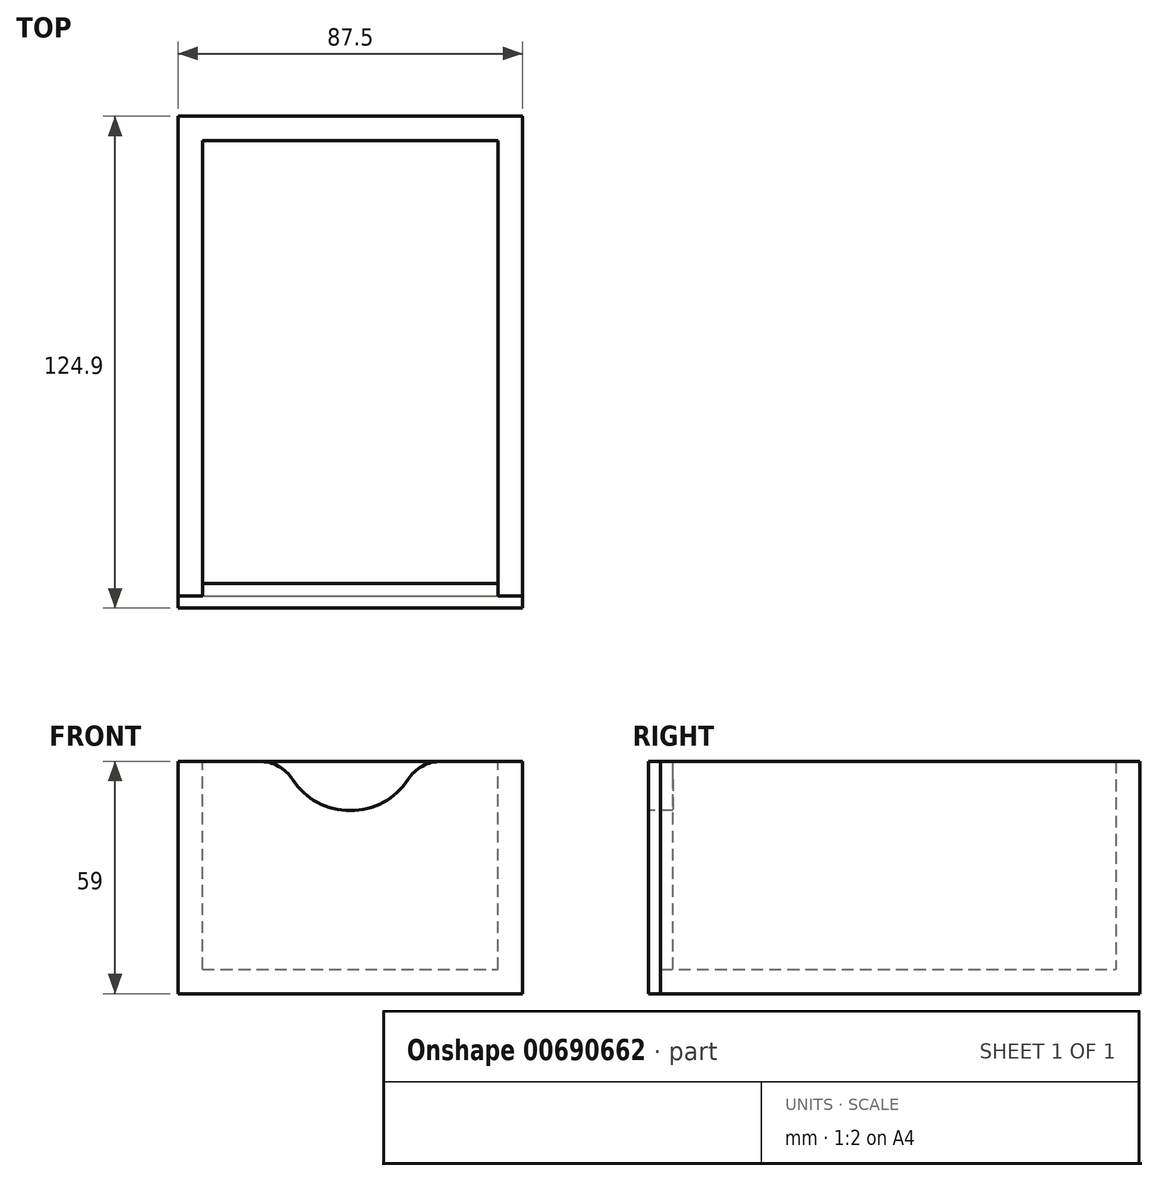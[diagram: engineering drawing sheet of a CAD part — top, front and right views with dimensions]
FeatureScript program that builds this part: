
annotation { "Feature Type Name" : "Feature", "Feature Type Description" : "" }
export const myFeature = defineFeature(function(context is Context, id is Id, definition is map)
    precondition{}
    {
        {
            var Q0;
            Q0=qCreatedBy(makeId("Front.planeOp"),FACE);
            var sketch = newSketch(context, id + "F0", { "sketchPlane" : qUnion([Q0])});
            skLineSegment(sketch, "E0.bottom", {"start": v(0, 0) * mm, "end": v(87.5, 0) * mm});
            skLineSegment(sketch, "E0.top", {"start": v(0, 59) * mm, "end": v(87.5, 59) * mm});
            skLineSegment(sketch, "E0.left", {"start": v(0, 0) * mm, "end": v(0, 59) * mm});
            skLineSegment(sketch, "E0.right", {"start": v(87.5, 0) * mm, "end": v(87.5, 59) * mm});
            skSolve(sketch);
        }
        {
            var Q0;
            Q0=qSketchRegion(id+"F0",true);
            extrude(context, id + "F1", {"entities" : qUnion([Q0]), "depth" : 6.2 * mm, "offsetDistance" : 25 * mm});
        }
        {
            var Q0;
            Q0=makeQuery(id+"F0.imprint","IMPRINT",FACE,{"disambiguationData":[TD([[makeQuery(id+"F0.imprint","IMPRINT",EDGE,{"derivedFrom":sQuery(id+"F0.wireOp",EDGE,"E0.bottom")}),1.0]])]});
            var sketch = newSketch(context, id + "F2", { "sketchPlane" : qUnion([Q0])});
            skLineSegment(sketch, "E1.bottom", {"start": v(87.5, 0) * mm, "end": v(0, 0) * mm});
            skLineSegment(sketch, "E1.top", {"start": v(87.5, 6.2) * mm, "end": v(0, 6.2) * mm});
            skLineSegment(sketch, "E1.left", {"start": v(87.5, 0) * mm, "end": v(87.5, 6.2) * mm});
            skLineSegment(sketch, "E1.right", {"start": v(0, 0) * mm, "end": v(0, 6.2) * mm});
            skLineSegment(sketch, "E2.bottom", {"start": v(0, 6.2) * mm, "end": v(6.2, 6.2) * mm});
            skLineSegment(sketch, "E2.top", {"start": v(0, 67.97) * mm, "end": v(6.2, 67.97) * mm});
            skLineSegment(sketch, "E2.left", {"start": v(0, 6.2) * mm, "end": v(0, 67.97) * mm});
            skLineSegment(sketch, "E2.right", {"start": v(6.2, 6.2) * mm, "end": v(6.2, 67.97) * mm});
            skLineSegment(sketch, "E3.bottom", {"start": v(87.5, 6.2) * mm, "end": v(81.3, 6.2) * mm});
            skLineSegment(sketch, "E3.top", {"start": v(87.5, 59) * mm, "end": v(81.3, 59) * mm});
            skLineSegment(sketch, "E3.left", {"start": v(87.5, 6.2) * mm, "end": v(87.5, 59) * mm});
            skLineSegment(sketch, "E3.right", {"start": v(81.3, 6.2) * mm, "end": v(81.3, 59) * mm});
            skSolve(sketch);
        }
        {
            var Q0;
            Q0=qSketchRegion(id+"F2",true);
            extrude(context, id + "F3", {"entities" : qUnion([Q0]), "operationType" : NewBodyOperationType.REMOVE, "depth" : 3.1 * mm, "offsetDistance" : 25 * mm});
        }
        {
            var Q0;
            Q0=makeQuery(id+"F1.opExtrude","SWEPT_FACE",FACE,{"disambiguationData":[OSD([sQuery(id+"F0.wireOp",EDGE,"E0.bottom")])]});
            var sketch = newSketch(context, id + "F4", { "sketchPlane" : qUnion([Q0])});
            skLineSegment(sketch, "E4.bottom", {"start": v(0, 3.1) * mm, "end": v(87.5, 3.1) * mm});
            skLineSegment(sketch, "E4.top", {"start": v(0, -115.6) * mm, "end": v(87.5, -115.6) * mm});
            skLineSegment(sketch, "E4.left", {"start": v(0, 3.1) * mm, "end": v(0, -115.6) * mm});
            skLineSegment(sketch, "E4.right", {"start": v(87.5, 3.1) * mm, "end": v(87.5, -115.6) * mm});
            skSolve(sketch);
        }
        {
            var Q0;
            Q0=qSketchRegion(id+"F4",true);
            extrude(context, id + "F5", {"entities" : qUnion([Q0]), "oppositeDirection" : true, "depth" : 6.2 * mm, "offsetDistance" : 25 * mm});
        }
        {
            var Q0;
            Q0=makeQuery(id+"F5.opExtrude","CAP_FACE",FACE,{"disambiguationData":[OSD([sQuery(id+"F4.wireOp",EDGE,"E4.bottom"),sQuery(id+"F4.wireOp",EDGE,"E4.top"),sQuery(id+"F4.wireOp",EDGE,"E4.left"),sQuery(id+"F4.wireOp",EDGE,"E4.right")])],"isStart":false});
            var sketch = newSketch(context, id + "F6", { "sketchPlane" : qUnion([Q0])});
            skLineSegment(sketch, "E5.bottom", {"start": v(0, -3.1) * mm, "end": v(6.2, -3.1) * mm});
            skLineSegment(sketch, "E5.top", {"start": v(0, 115.6) * mm, "end": v(6.2, 115.6) * mm});
            skLineSegment(sketch, "E5.left", {"start": v(0, -3.1) * mm, "end": v(0, 115.6) * mm});
            skLineSegment(sketch, "E5.right", {"start": v(6.2, -3.1) * mm, "end": v(6.2, 115.6) * mm});
            skLineSegment(sketch, "E6.bottom", {"start": v(87.5, -3.1) * mm, "end": v(81.3, -3.1) * mm});
            skLineSegment(sketch, "E6.top", {"start": v(87.5, 115.6) * mm, "end": v(81.3, 115.6) * mm});
            skLineSegment(sketch, "E6.left", {"start": v(87.5, -3.1) * mm, "end": v(87.5, 115.6) * mm});
            skLineSegment(sketch, "E6.right", {"start": v(81.3, -3.1) * mm, "end": v(81.3, 115.6) * mm});
            skSolve(sketch);
        }
        {
            var Q0;
            Q0=qSketchRegion(id+"F6",true);
            extrude(context, id + "F7", {"entities" : qUnion([Q0]), "operationType" : NewBodyOperationType.REMOVE, "oppositeDirection" : true, "depth" : 3.1 * mm, "offsetDistance" : 25 * mm});
        }
        {
            var Q0;
            Q0=makeQuery(id+"F5.opExtrude","SWEPT_FACE",FACE,{"disambiguationData":[OSD([sQuery(id+"F4.wireOp",EDGE,"E4.left")])]});
            var sketch = newSketch(context, id + "F8", { "sketchPlane" : qUnion([Q0])});
            skLineSegment(sketch, "E7.bottom", {"start": v(-115.6, 3.1) * mm, "end": v(3.1, 3.1) * mm});
            skLineSegment(sketch, "E7.top", {"start": v(-115.6, 59) * mm, "end": v(3.1, 59) * mm});
            skLineSegment(sketch, "E7.left", {"start": v(-115.6, 3.1) * mm, "end": v(-115.6, 59) * mm});
            skLineSegment(sketch, "E7.right", {"start": v(3.1, 3.1) * mm, "end": v(3.1, 59) * mm});
            skSolve(sketch);
        }
        {
            var Q0;
            Q0=qSketchRegion(id+"F8",true);
            extrude(context, id + "F9", {"entities" : qUnion([Q0]), "oppositeDirection" : true, "depth" : 6.2 * mm, "offsetDistance" : 25 * mm});
        }
        {
            var Q0;
            Q0=makeQuery(id+"F9.opExtrude","SWEPT_BODY",BODY,{"disambiguationData":[OSD([sQuery(id+"F8.wireOp",EDGE,"E7.bottom"),sQuery(id+"F8.wireOp",EDGE,"E7.top"),sQuery(id+"F8.wireOp",EDGE,"E7.left"),sQuery(id+"F8.wireOp",EDGE,"E7.right")])]});
            transform(context, id + "F10", {"entities" : qUnion([Q0]), "transformType" : TransformType.TRANSLATION_3D, "dx" : 81.3 * mm, "dy" : 0 * mm, "dz" : 0 * mm, "makeCopy" : true});
        }
        {
            var Q0;
            Q0=makeQuery(id+"F5.opExtrude","SWEPT_FACE",FACE,{"disambiguationData":[OSD([sQuery(id+"F4.wireOp",EDGE,"E4.top")])]});
            var sketch = newSketch(context, id + "F11", { "sketchPlane" : qUnion([Q0])});
            skLineSegment(sketch, "E8.bottom", {"start": v(-87.5, 0) * mm, "end": v(0, 0) * mm});
            skLineSegment(sketch, "E8.top", {"start": v(-87.5, 59) * mm, "end": v(0, 59) * mm});
            skLineSegment(sketch, "E8.left", {"start": v(-87.5, 0) * mm, "end": v(-87.5, 59) * mm});
            skLineSegment(sketch, "E8.right", {"start": v(0, 0) * mm, "end": v(0, 59) * mm});
            skSolve(sketch);
        }
        {
            var Q0;
            Q0=qSketchRegion(id+"F11",true);
            extrude(context, id + "F12", {"entities" : qUnion([Q0]), "depth" : 3.1 * mm, "offsetDistance" : 25 * mm});
        }
        {
            var Q0;
            Q0=makeQuery(id+"F12.opExtrude","CAP_FACE",FACE,{"disambiguationData":[OSD([sQuery(id+"F11.wireOp",EDGE,"E8.bottom"),sQuery(id+"F11.wireOp",EDGE,"E8.top"),sQuery(id+"F11.wireOp",EDGE,"E8.left"),sQuery(id+"F11.wireOp",EDGE,"E8.right")])],"isStart":true});
            var sketch = newSketch(context, id + "F13", { "sketchPlane" : qUnion([Q0])});
            skLineSegment(sketch, "E9.bottom", {"start": v(6.2, 59) * mm, "end": v(81.3, 59) * mm});
            skLineSegment(sketch, "E9.top", {"start": v(6.2, 6.2) * mm, "end": v(81.3, 6.2) * mm});
            skLineSegment(sketch, "E9.left", {"start": v(6.2, 59) * mm, "end": v(6.2, 6.2) * mm});
            skLineSegment(sketch, "E9.right", {"start": v(81.3, 59) * mm, "end": v(81.3, 6.2) * mm});
            skSolve(sketch);
        }
        {
            var Q0;
            Q0=qSketchRegion(id+"F13",true);
            extrude(context, id + "F14", {"entities" : qUnion([Q0]), "operationType" : NewBodyOperationType.ADD, "depth" : 3.1 * mm, "offsetDistance" : 25 * mm});
        }
        {
            var Q0;
            Q0=makeQuery(id+"F1.opExtrude","CAP_FACE",FACE,{"disambiguationData":[OSD([sQuery(id+"F0.wireOp",EDGE,"E0.bottom"),sQuery(id+"F0.wireOp",EDGE,"E0.top"),sQuery(id+"F0.wireOp",EDGE,"E0.left"),sQuery(id+"F0.wireOp",EDGE,"E0.right")])],"isStart":false});
            var sketch = newSketch(context, id + "F15", { "sketchPlane" : qUnion([Q0])});
            skCircle(sketch, "E10", {"center": v(43.75, 64) * mm, "radius": 17.5 * mm});
            skPoint(sketch, "E10.centerSnap0", {"position": v(43.75, 59) * mm});
            skSolve(sketch);
        }
        {
            var Q0;
            Q0=qSketchRegion(id+"F15",true);
            extrude(context, id + "F16", {"entities" : qUnion([Q0]), "operationType" : NewBodyOperationType.REMOVE, "oppositeDirection" : true, "depth" : 25 * mm, "offsetDistance" : 25 * mm});
        }
        {
            var Q0;
            Q0=makeQuery(id+"F16.boolean.opBoolean","INTERSECT",EDGE,{"disambiguationData":[OD(1.0)],"derivedFrom":[makeQuery(id+"F1.opExtrude","SWEPT_FACE",FACE,{"disambiguationData":[OSD([sQuery(id+"F0.wireOp",EDGE,"E0.top")])]}),makeQuery(id+"F16.opExtrude","SWEPT_FACE",FACE,{"disambiguationData":[OSD([sQuery(id+"F15.wireOp",EDGE,"E10")])]})]});
            var Q1;
            Q1=makeQuery(id+"F16.boolean.opBoolean","INTERSECT",EDGE,{"disambiguationData":[OD(0.0)],"derivedFrom":[makeQuery(id+"F1.opExtrude","SWEPT_FACE",FACE,{"disambiguationData":[OSD([sQuery(id+"F0.wireOp",EDGE,"E0.top")])]}),makeQuery(id+"F16.opExtrude","SWEPT_FACE",FACE,{"disambiguationData":[OSD([sQuery(id+"F15.wireOp",EDGE,"E10")])]})]});
            fillet(context, id + "F17", {"entities" : qUnion([Q0, Q1]), "radius" : 10 * mm, "tangentPropagation" : true, "allowEdgeOverflow" : false});
        }
    });
